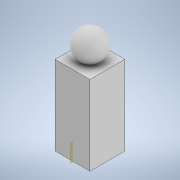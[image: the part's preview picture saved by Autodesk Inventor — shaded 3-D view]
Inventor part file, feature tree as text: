
AUTODESK INVENTOR PART (.ipt)
format: ipt  version: 2021 (Build 250183000, 183)  size: 119,808 bytes
history: native  units: in
note: dims shown in document units (in); Inventor stores cm internally (conversion verified against a paired STEP export)
features: sketch x2, extrude x1, plane x1, revolve x1
ambient origin geometry x8: Origin, YZ Plane, XZ Plane, XY Plane, X Axis, Y Axis, Z Axis, Center Point
bodies: Body1 (feature_tree)
feature tree (5):
  extrude  "Extrusion3"  Depth=0.8661in
  plane  "Work Plane1"
  revolve  "Revolution2"  [1 undecoded]
  sketch  "Sketch6"  dims[d18=0.8661in d19=0.8661in]
  sketch  "Sketch8"  dims[d20=1.9685in d21=0.0in d27=-0.4331in d30=0.315in d31=0.7087in d32=360.0deg]
note: 1 required parameter value undecoded (feature->parameter linkage not recoverable at this tier; creation-order binding heuristic only, values carry confidence <= 0.55)
